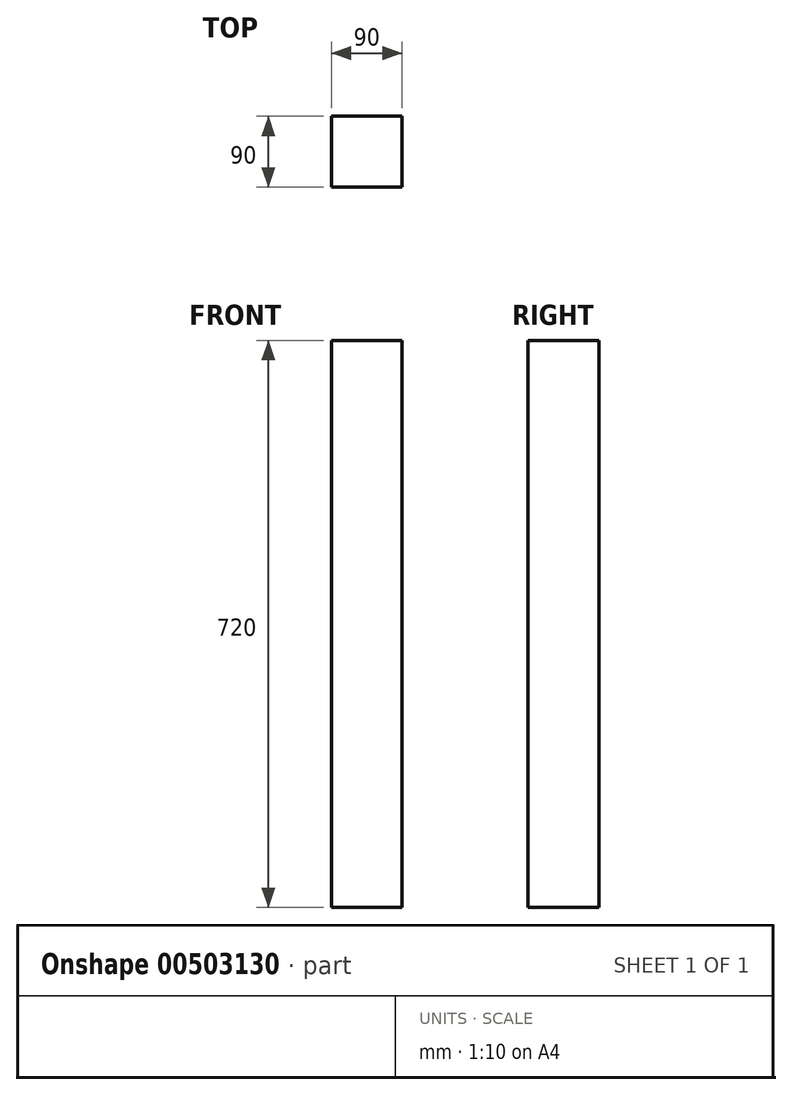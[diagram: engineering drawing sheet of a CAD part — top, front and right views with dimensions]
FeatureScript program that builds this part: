
annotation { "Feature Type Name" : "Feature", "Feature Type Description" : "" }
export const myFeature = defineFeature(function(context is Context, id is Id, definition is map)
    precondition{}
    {
        {
            var Q0;
            Q0=qCreatedBy(makeId("Top.planeOp"),FACE);
            var sketch = newSketch(context, id + "F0", { "sketchPlane" : qUnion([Q0])});
            skLineSegment(sketch, "E0.bottom", {"start": v(-45, 45) * mm, "end": v(45, 45) * mm});
            skLineSegment(sketch, "E0.top", {"start": v(-45, -45) * mm, "end": v(45, -45) * mm});
            skLineSegment(sketch, "E0.left", {"start": v(-45, 45) * mm, "end": v(-45, -45) * mm});
            skLineSegment(sketch, "E0.right", {"start": v(45, 45) * mm, "end": v(45, -45) * mm});
            skSolve(sketch);
        }
        {
            var Q0;
            Q0=makeQuery(id+"F0.imprint","IMPRINT",FACE,{"disambiguationData":[TD([[makeQuery(id+"F0.imprint","IMPRINT",EDGE,{"derivedFrom":sQuery(id+"F0.wireOp",EDGE,"E0.bottom")}),-1.0]])]});
            extrude(context, id + "F1", {"entities" : qUnion([Q0]), "depth" : (850 - 30 - 100) * mm, "offsetDistance" : 25 * mm});
        }
        {
            var Q0;
            Q0=makeQuery(id+"F1.opExtrude","SWEPT_FACE",FACE,{"disambiguationData":[OSD([sQuery(id+"F0.wireOp",EDGE,"E0.top")])]});
            var sketch = newSketch(context, id + "F2", { "sketchPlane" : qUnion([Q0])});
            skLineSegment(sketch, "E1", {"start": v(-45, 80) * mm, "end": v(45, 80) * mm, "construction": true});
            skSolve(sketch);
        }
    });
